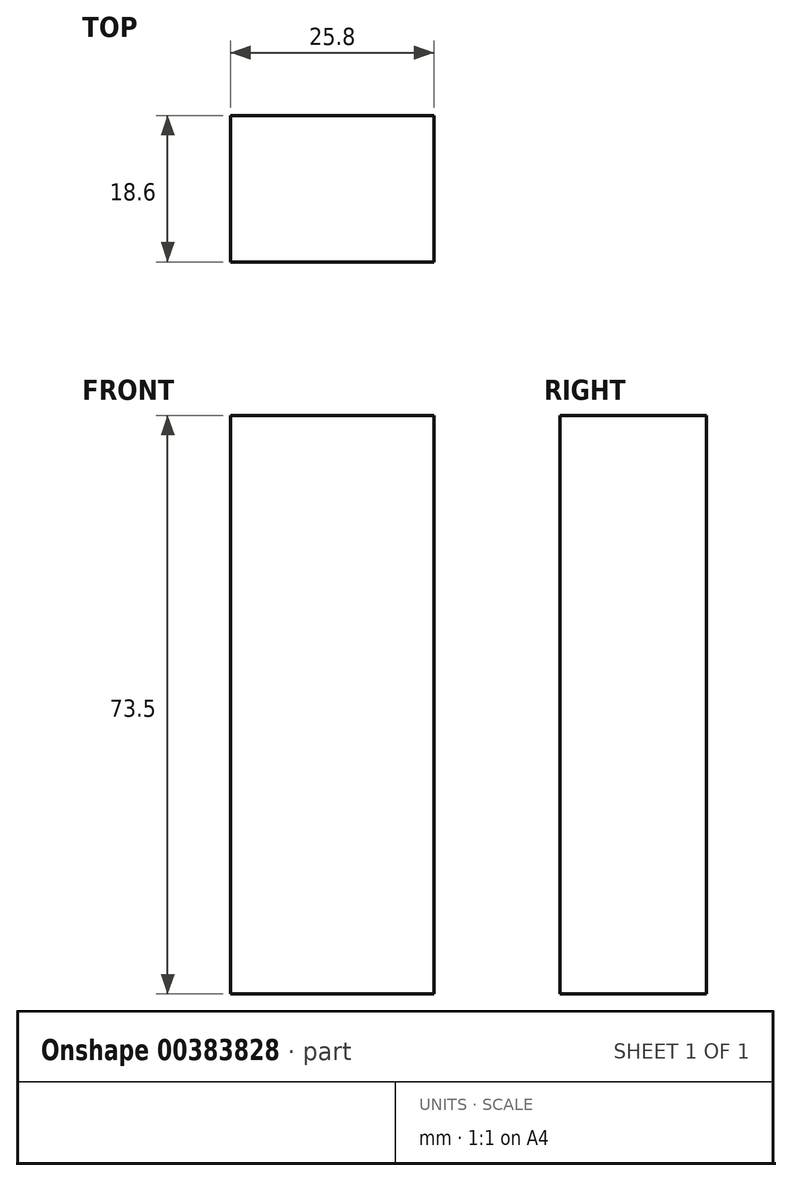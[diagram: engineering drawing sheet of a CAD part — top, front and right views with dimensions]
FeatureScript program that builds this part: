
annotation { "Feature Type Name" : "Feature", "Feature Type Description" : "" }
export const myFeature = defineFeature(function(context is Context, id is Id, definition is map)
    precondition{}
    {
        {
            var Q0;
            Q0=qCreatedBy(makeId("Front.planeOp"),FACE);
            var sketch = newSketch(context, id + "F0", { "sketchPlane" : qUnion([Q0])});
            skLineSegment(sketch, "E0.bottom", {"start": v(12.9, 36.75) * mm, "end": v(-12.9, 36.75) * mm});
            skLineSegment(sketch, "E0.top", {"start": v(12.9, -36.75) * mm, "end": v(-12.9, -36.75) * mm});
            skLineSegment(sketch, "E0.left", {"start": v(12.9, 36.75) * mm, "end": v(12.9, -36.75) * mm});
            skLineSegment(sketch, "E0.right", {"start": v(-12.9, 36.75) * mm, "end": v(-12.9, -36.75) * mm});
            skPoint(sketch, "E0.middle", {"position": v(0, 0) * mm});
            skSolve(sketch);
        }
        {
            var Q0;
            Q0 = qSketchRegion(id + "F0", true);
            extrude(context, id + "F1", {"entities" : qUnion([Q0]), "depth" : (18.6 / 2) * mm, "hasSecondDirection" : true, "secondDirectionOppositeDirection" : true, "secondDirectionDepth" : (18.6 / 2) * mm});
        }
    });
